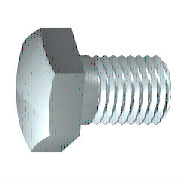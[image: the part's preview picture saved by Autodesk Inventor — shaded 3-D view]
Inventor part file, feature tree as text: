
AUTODESK INVENTOR PART (.ipt)
format: ipt  version: 2023.2 (Build 272271030, 271C)  size: 192,000 bytes
history: native  units: mm (DEFAULTED — no unit token found)
features: sketch x3, extrude x1, chamfer x1, plane x1
ambient origin geometry x7: Origin, YZ Plane, XZ Plane, X Axis, Y Axis, Z Axis, Center Point
bodies: Solid1 (feature_tree), Body (feature_tree)
feature tree (6):
  extrude  "Head"  Depth=45.5mm
  chamfer  "Chamfer1"  Distance=5.8mm
  plane  "Work Plane1"
  sketch  "Sketch1"  dims[d0=50.0mm d1=45.5mm]
  sketch  "Sketch2"  dims[d2=10.0mm]
  sketch  "Sketch4"  dims[d12=90.0deg d3=5.8mm d4=0.0mm d5=30.0deg d21=90.0deg d6=0.920175mm d7=0.920275mm d8=0.0mm d9=0.6001mm d10=14.63mm d11=16.0mm d13=0.920275mm d14=10.0mm d15=45.5mm d16=0.0mm d19=16.0mm d55=45.0deg d57=0.0mm d58=0.0mm]
